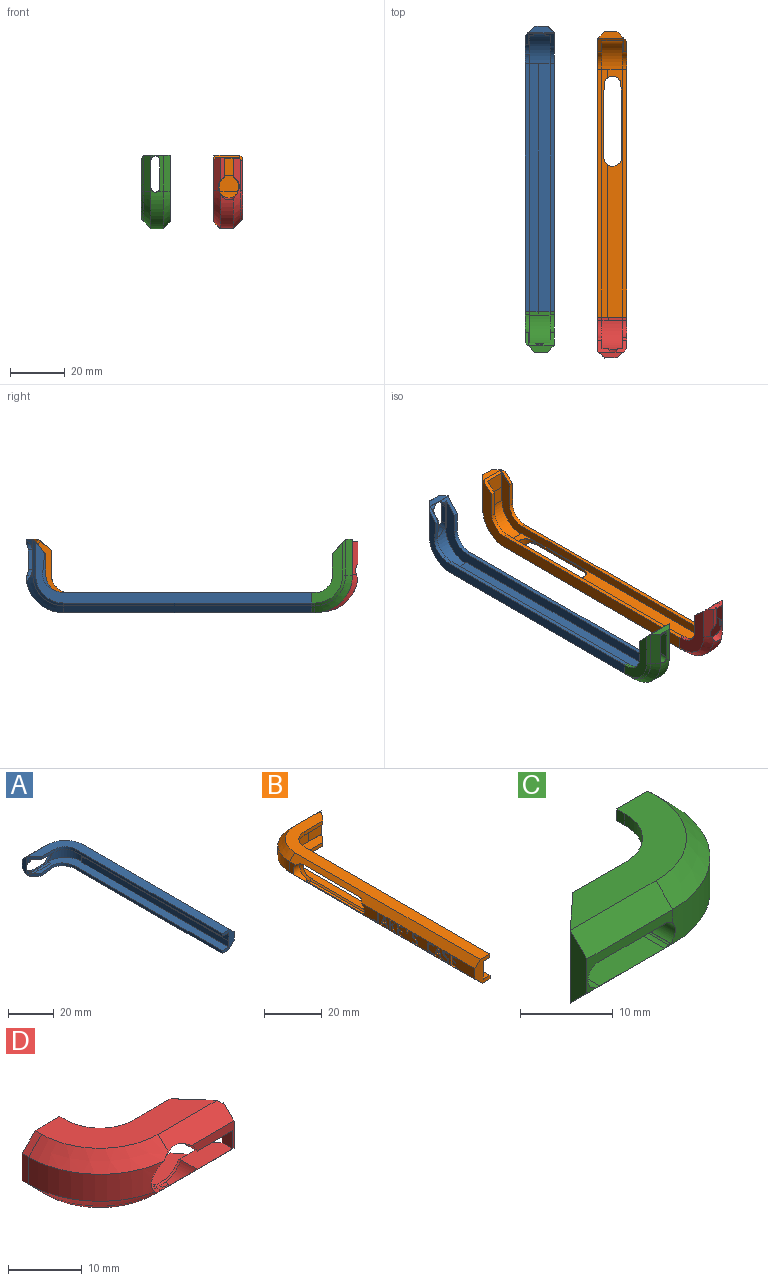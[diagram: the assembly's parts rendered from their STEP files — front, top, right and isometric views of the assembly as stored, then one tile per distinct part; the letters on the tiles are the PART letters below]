
ASSEMBLY  parts=4 mates=2
PART A: 62 faces, bbox 27.2x104.7x11 mm
  f0: bspline ~1.52x1.52mm, area 0mm2, adj f8,f47,f60
  f1: plane 100.84x22.1mm, normal (0,0,-1), area 419.9mm2, adj f2,f3,f4,f27,f28,f54,f55,f56
  f2: plane 5x4.28mm, normal (-0.65,-0.76,0), area 7.6mm2, adj f1,f14,f39,f41,f50,f53,f54,f58
  f3: plane 7.21x1.5mm, normal (0.09,-1,0), area 10.9mm2, adj f1,f4,f5,f17,f58
  f4: cylinder r=5.99mm len=6.33mm, axis (0,0,-1), area 12.5mm2, adj f1,f3,f17,f27
  f5: plane 9.31x5.51mm, normal (-0.65,-0.76,0), area 18.4mm2, adj f3,f6,f7,f11,f12,f15,f16,f17
  f6: cone r=2.27mm half-angle=45deg, axis (0,1,0), area 1.1mm2, adj f5,f9,f12,f47
  f7: plane 10.51x0.06mm, normal (0,-1,0), area 0.7mm2, adj f5,f17,f44,f46
  f8: cone r=2.27mm half-angle=45deg, axis (0,1,0), area 0.6mm2, adj f0,f9,f36,f47
  f9: plane 7.3x0.23mm, normal (0,0.71,-0.71), area 2.4mm2, adj f6,f8,f35,f47
  f10: bspline ~1.51x1.49mm, area 0mm2, adj f26,f42,f44
  f11: cone r=2.27mm half-angle=45deg, axis (0,1,0), area 1.1mm2, adj f5,f12,f25,f43,f46
  f12: cylinder r=3.77mm len=7.53mm, axis (0,1,0), area 28.3mm2, adj f5,f6,f11,f34,f35,f38,f39,f40
  f13: plane 93.02x0.26mm, normal (0,0,-1), area 0.3mm2, adj f31,f32,f51,f52,f57
  f14: plane 0.08x0.04mm, normal (0,0,-1), area 0mm2, adj f2,f20,f39,f41
  f15: plane 101.7x23.07mm, normal (0,0,-1), area 452.5mm2, adj f5,f16,f29,f30,f47,f49,f57,f59
  f16: plane 7.49x1.52mm, normal (0,-1,0), area 11.4mm2, adj f5,f15,f18,f29
  f17: plane 101.7x21.59mm, normal (0,0,1), area 433.3mm2, adj f3,f4,f5,f7,f27,f28,f44,f45
  f18: plane 101.81x24.18mm, normal (0,0,1), area 542.6mm2, adj f5,f16,f24,f29,f30,f37,f38,f57
  f19: plane 0.08x0.06mm, normal (0,0,1), area 0mm2, adj f20,f38,f41
  f20: plane 9.57x2.62mm, normal (-1,0,0), area 18.7mm2, adj f14,f19,f38,f39,f40,f41
  f21: plane 90.62x4.49mm, normal (1,0,0), area 407.2mm2, adj f23,f24,f31,f57
  f22: bspline ~6.5x3.4mm, area 20.5mm2, adj f23,f32,f33,f36,f37,f61
  f23: cylinder r=13.72mm len=13.71mm, axis (0,0,-1), area 86.3mm2, adj f21,f22,f32,f37
  f24: plane 90.62x2.54mm, normal (0.71,0,0.71), area 325.5mm2, adj f18,f21,f37,f57
  f25: plane 7.3x0.27mm, normal (0,0.71,0.71), area 2.8mm2, adj f11,f26,f34,f46
  f26: cone r=2.27mm half-angle=45deg, axis (0,1,0), area 0.6mm2, adj f10,f25,f33,f42,f46
  f27: cylinder r=6.38mm len=3.23mm, axis (0,0,-1), area 5.1mm2, adj f1,f4,f17,f28
  f28: plane 90.62x1.5mm, normal (-1,0,0), area 135.9mm2, adj f1,f17,f27,f57
  f29: cylinder r=6.46mm len=6.46mm, axis (0,0,1), area 15.5mm2, adj f15,f16,f18,f30
  f30: plane 90.62x1.52mm, normal (-1,0,0), area 138.1mm2, adj f15,f18,f29,f57
  f31: plane 90.62x2.54mm, normal (0.71,0,-0.71), area 325.5mm2, adj f13,f21,f32,f57
  f32: cone r=13.72mm half-angle=45deg, axis (0,0,1), area 67.4mm2, adj f13,f22,f23,f31,f39,f51
  f33: cylinder r=3.77mm len=1.9mm, axis (0,1,0), area 2.4mm2, adj f22,f26,f34,f39,f44
  f34: plane 7.3x0.93mm, normal (0,0,1), area 6.8mm2, adj f12,f25,f33,f39
  f35: plane 7.3x2.38mm, normal (0,0,-1), area 17.4mm2, adj f9,f12,f36,f38
  f36: cylinder r=3.77mm len=2.9mm, axis (0,1,0), area 5.3mm2, adj f8,f22,f35,f38,f60
  f37: cone r=13.72mm half-angle=45deg, axis (0,0,-1), area 70.2mm2, adj f18,f22,f23,f24,f38
  f38: plane 13.44x2.92mm, normal (0,0.71,0.71), area 35.3mm2, adj f12,f18,f19,f20,f35,f36,f37,f40
  f39: plane 13.31x2.79mm, normal (0,0.71,-0.71), area 10mm2, adj f2,f12,f14,f20,f32,f33,f34,f40
  f40: plane 4.49x1.55mm, normal (0,1,0), area 1.9mm2, adj f12,f20,f38,f39
  f41: plane 9.57x0.08mm, normal (0.82,-0.58,0), area 1mm2, adj f2,f5,f14,f19,f20,f53
  f42: plane 1.39x0.51mm, normal (0,-1,0), area 0.3mm2, adj f10,f26,f44,f46
  f43: plane 2.28x1.32mm, normal (0,-1,0), area 1.1mm2, adj f5,f11,f46
  f44: plane 2.04x0.57mm, normal (1,0,0), area 0.3mm2, adj f7,f10,f17,f33,f42,f46,f61
  f45: plane 90.62x3.23mm, normal (-1,0,0), area 292.5mm2, adj f17,f48,f57,f59
  f46: plane 12.01x1.3mm, normal (0,0,1), area 14mm2, adj f5,f7,f11,f25,f26,f42,f43,f44
  f47: plane 11.99x1.82mm, normal (0,-1,0), area 6.9mm2, adj f0,f5,f6,f8,f9,f15,f60
  f48: plane 90.62x0.01mm, normal (0,0,1), area 1mm2, adj f45,f49,f57,f59
  f49: plane 90.62x4.32mm, normal (-1,0,0), area 391.6mm2, adj f15,f48,f57,f59
  f50: plane 13.05x0.02mm, normal (0,1,0), area 0.3mm2, adj f2,f39,f51,f54
  f51: cylinder r=11.18mm len=11.2mm, axis (0,0,-1), area 0.3mm2, adj f13,f32,f50,f52,f55
  f52: plane 90.62x0.01mm, normal (1,0,0), area 0.9mm2, adj f13,f51,f56,f57
  f53: plane 4.97x4.27mm, normal (0,0,1), area 0.2mm2, adj f2,f5,f41,f58
  f54: plane 13.05x0.99mm, normal (0,0.71,-0.71), area 17.5mm2, adj f1,f2,f50,f55
  f55: cone r=10.19mm half-angle=45deg, axis (0,0,1), area 23.5mm2, adj f1,f51,f54,f56
  f56: plane 90.62x0.99mm, normal (0.71,0,-0.71), area 127mm2, adj f1,f52,f55,f57
  f57: plane 10.57x7.35mm, normal (0,-1,0), area 38.3mm2, adj f1,f13,f15,f17,f18,f21,f24,f28
  f58: plane 1.27x0.02mm, normal (0.93,-0.38,0), area 0mm2, adj f1,f2,f3,f53
  f59: plane 7.55x0.76mm, normal (0,1,0), area 5.7mm2, adj f15,f17,f45,f48,f49,f61
  f60: plane 1x0.77mm, normal (1,0,0), area 0.6mm2, adj f0,f15,f36,f47,f61
  f61: cylinder r=11.08mm len=11.08mm, axis (0,0,-1), area 120.9mm2, adj f15,f17,f22,f44,f59,f60
PART B: 215 faces, bbox 27.9x105.4x11.6 mm
  f0: cone r=2.74mm half-angle=45deg, axis (-1,0,0), area 1.8mm2, adj f2,f3,f25,f29,f204,f213
  f1: cone r=2.74mm half-angle=45deg, axis (-1,0,0), area 15.3mm2, adj f2,f10,f25,f30,f191,f212,f213,f214
  f2: bspline ~24.21x1.5mm, area 25.1mm2, adj f0,f1,f25,f213
  f3: cone r=4.02mm half-angle=45deg, axis (-1,0,0), area 15.3mm2, adj f0,f9,f201,f202,f203,f204,f211,f213
  f4: plane 10.64x7.55mm, normal (0,-1,0), area 44.6mm2, adj f5,f20,f23,f200,f207,f209
  f5: plane 0.96x0.83mm, normal (-0.65,-0.76,0), area 0mm2, adj f4,f6,f23,f209
  f6: plane 9.3x4.81mm, normal (0.76,-0.65,0), area 18.8mm2, adj f5,f20,f22,f23,f28,f35,f43,f187
  f7: plane 0.96x0.83mm, normal (-0.65,-0.76,0), area 0.5mm2, adj f40,f43,f206
  f8: cylinder r=4.24mm len=0.93mm, axis (-1,0,0), area 0.1mm2, adj f9,f31,f38,f190,f191,f201
  f9: cone r=2.74mm half-angle=45deg, axis (-1,0,0), area 1.5mm2, adj f3,f8,f10,f191,f201,f214
  f10: plane 24.21x0.54mm, normal (-0.71,0,0.71), area 18.6mm2, adj f1,f9,f191,f214
  f11: plane 9.26x4.52mm, normal (-1,0,0), area 22.7mm2, adj f18,f19,f44,f45,f46,f47,f48,f49
  f12: plane 26.97x4.53mm, normal (-1,0,0), area 83.9mm2, adj f18,f19,f30,f80,f81,f82,f83,f84
  f13: plane 8.56x4.55mm, normal (-1,0,0), area 26mm2, adj f18,f19,f75,f76,f77,f78,f90,f91
  f14: plane 15.15x4.52mm, normal (-1,0,0), area 56.3mm2, adj f18,f19,f54,f55,f56,f57,f58,f59
  f15: plane 2.38x1.38mm, normal (-1,0,0), area 2.7mm2, adj f19,f175,f181,f182
  f16: plane 2.38x1.38mm, normal (-1,0,0), area 2.7mm2, adj f19,f161,f167,f168
  f17: plane 2.13x1.8mm, normal (-1,0,0), area 2.3mm2, adj f19,f143,f154,f155
  f18: plane 91.1x3.02mm, normal (-0.71,0,0.71), area 281.3mm2, adj f11,f12,f13,f14,f22,f25,f29,f30
  f19: plane 57.25x2.6mm, normal (-0.71,0,-0.71), area 198.6mm2, adj f11,f12,f13,f14,f15,f16,f17,f24
  f20: plane 100.95x21.93mm, normal (0,0,1), area 381.4mm2, adj f4,f6,f35,f36,f37,f196,f199,f200
  f21: plane 100.81x22.43mm, normal (0,0,-1), area 436.2mm2, adj f35,f36,f37,f192,f193,f194,f195,f196
  f22: plane 101.81x23.53mm, normal (0,0,1), area 545.6mm2, adj f6,f18,f26,f27,f28,f41,f42,f196
  f23: plane 100.94x21.93mm, normal (0,0,-1), area 373.5mm2, adj f4,f5,f6,f26,f27,f28,f196,f199
  f24: plane 57.18x0mm, normal (0,0,-1), area 0mm2, adj f19,f30,f190,f196
  f25: plane 27.07x2.41mm, normal (0,0,-1), area 64.9mm2, adj f0,f1,f2,f18,f29,f30
  f26: plane 90.62x1.52mm, normal (1,0,0), area 138.1mm2, adj f22,f23,f27,f196
  f27: cylinder r=6.45mm len=6.46mm, axis (0,0,1), area 15.5mm2, adj f22,f23,f26,f28
  f28: plane 9.01x1.52mm, normal (0,-1,0), area 13.7mm2, adj f6,f22,f23,f27
  f29: cylinder r=4.24mm len=2.17mm, axis (-1,0,0), area 0.1mm2, adj f0,f18,f25,f202
  f30: cylinder r=4.24mm len=8.05mm, axis (-1,0,0), area 26.5mm2, adj f1,f12,f18,f19,f24,f25,f190,f191
  f31: plane 24.24x17.98mm, normal (0,0,-1), area 0.1mm2, adj f8,f38,f39,f40,f188,f189,f190,f197
  f32: plane 13.06x4.49mm, normal (0,1,0), area 58.7mm2, adj f34,f40,f41,f43
  f33: plane 4.49x3mm, normal (-1,0,0), area 9.1mm2, adj f18,f34,f38,f203
  f34: cylinder r=13.72mm len=13.73mm, axis (0,0,-1), area 96.9mm2, adj f32,f33,f39,f42
  f35: plane 8.93x1.5mm, normal (0,-1,0), area 13.4mm2, adj f6,f20,f21,f37,f192
  f36: plane 90.62x1.5mm, normal (1,0,0), area 135.9mm2, adj f20,f21,f37,f196
  f37: cylinder r=6.38mm len=6.38mm, axis (0,0,-1), area 15mm2, adj f20,f21,f35,f36
  f38: plane 7.82x3.57mm, normal (-0.71,0,-0.71), area 12.4mm2, adj f8,f31,f33,f39,f201,f203
  f39: cone r=13.72mm half-angle=45deg, axis (0,0,1), area 70.3mm2, adj f31,f34,f38,f40
  f40: plane 13.06x2.54mm, normal (0,0.71,-0.71), area 46.5mm2, adj f7,f31,f32,f39,f43,f187,f197,f206
  f41: plane 13.06x2.54mm, normal (0,0.71,0.71), area 45.9mm2, adj f22,f32,f42,f43,f198,f205
  f42: cone r=13.72mm half-angle=45deg, axis (0,0,-1), area 70.3mm2, adj f18,f22,f34,f41
  f43: plane 9.57x2.54mm, normal (1,0,0), area 17.9mm2, adj f6,f7,f32,f40,f41,f198
  f44: extruded ~1.07x0.76mm, area 0.9mm2, adj f11,f18,f45,f63,f64
  f45: extruded ~0.83x0.76mm, area 0.7mm2, adj f11,f44,f46,f64
  f46: extruded ~0.8x0.76mm, area 0.7mm2, adj f11,f45,f47,f64
  f47: extruded ~0.91x0.76mm, area 0.8mm2, adj f11,f46,f48,f64
  f48: extruded ~0.87x0.76mm, area 0.7mm2, adj f11,f47,f49,f64
  f49: extruded ~0.76x0.49mm, area 0.4mm2, adj f11,f48,f50,f64
  f50: extruded ~1.07x0.76mm, area 1.1mm2, adj f11,f49,f51,f64
  f51: extruded ~1.26x0.76mm, area 1mm2, adj f11,f50,f52,f64
  f52: plane 0.76x0.54mm, normal (0,-1,0), area 0.4mm2, adj f11,f51,f53,f64
  f53: extruded ~1.26x0.76mm, area 1mm2, adj f11,f19,f52,f54,f64
  f54: extruded ~1.2x0.76mm, area 0.9mm2, adj f14,f19,f53,f55,f64
  f55: extruded ~0.92x0.76mm, area 0.8mm2, adj f14,f54,f56,f64
  f56: extruded ~0.76x0.73mm, area 0.6mm2, adj f14,f55,f57,f64
  f57: extruded ~1x0.76mm, area 0.9mm2, adj f14,f56,f58,f64
  f58: extruded ~0.82x0.76mm, area 0.7mm2, adj f14,f57,f59,f64
  f59: extruded ~0.76x0.5mm, area 0.4mm2, adj f14,f58,f60,f64
  f60: extruded ~0.89x0.76mm, area 1mm2, adj f14,f59,f61,f64
  f61: extruded ~1.1x0.76mm, area 0.9mm2, adj f14,f60,f62,f64
  f62: plane 0.76x0.5mm, normal (0,0.93,0.36), area 0.4mm2, adj f14,f61,f63,f64
  f63: extruded ~1.27x0.76mm, area 1mm2, adj f14,f18,f44,f62,f64
  f64: plane 4.58x2.88mm, normal (-1,0,0), area 5mm2, adj f44,f45,f46,f47,f48,f49,f50,f51
  f65: extruded ~1.09x0.76mm, area 0.8mm2, adj f11,f19,f66,f78,f79
  f66: plane 0.76x0.49mm, normal (0,1,0), area 0.4mm2, adj f11,f65,f67,f79
  f67: extruded ~1x0.76mm, area 0.8mm2, adj f11,f66,f68,f79
  f68: extruded ~1.07x0.76mm, area 0.9mm2, adj f11,f67,f69,f79
  f69: extruded ~1.33x0.76mm, area 1.1mm2, adj f11,f68,f70,f79
  f70: extruded ~1.31x0.76mm, area 1.1mm2, adj f11,f69,f71,f79
  f71: extruded ~1.05x0.76mm, area 0.9mm2, adj f11,f70,f72,f79
  f72: extruded ~0.93x0.76mm, area 0.7mm2, adj f11,f71,f73,f79
  f73: plane 0.76x0.48mm, normal (0,0.89,0.45), area 0.4mm2, adj f11,f72,f74,f79
  f74: extruded ~1.17x0.76mm, area 0.9mm2, adj f11,f18,f73,f75,f79
  f75: extruded ~1.49x0.76mm, area 1.3mm2, adj f13,f18,f74,f76,f79
  f76: extruded ~1.67x0.76mm, area 1.4mm2, adj f13,f75,f77,f79
  f77: extruded ~1.7x0.76mm, area 1.4mm2, adj f13,f76,f78,f79
  f78: extruded ~1.44x0.76mm, area 1.2mm2, adj f13,f19,f65,f77,f79
  f79: plane 4.58x3.2mm, normal (-1,0,0), area 4.5mm2, adj f65,f66,f67,f68,f69,f70,f71,f72
  f80: extruded ~1.07x0.76mm, area 0.9mm2, adj f12,f18,f81,f99,f100
  f81: extruded ~0.83x0.76mm, area 0.7mm2, adj f12,f80,f82,f100
  f82: extruded ~0.8x0.76mm, area 0.7mm2, adj f12,f81,f83,f100
  f83: extruded ~0.91x0.76mm, area 0.8mm2, adj f12,f82,f84,f100
  f84: extruded ~0.87x0.76mm, area 0.7mm2, adj f12,f83,f85,f100
  f85: extruded ~0.76x0.49mm, area 0.4mm2, adj f12,f84,f86,f100
  f86: extruded ~1.07x0.76mm, area 1.1mm2, adj f12,f85,f87,f100
  f87: extruded ~1.26x0.76mm, area 1mm2, adj f12,f86,f88,f100
  f88: plane 0.76x0.54mm, normal (0,-1,0), area 0.4mm2, adj f12,f87,f89,f100
  f89: extruded ~1.26x0.76mm, area 1mm2, adj f12,f19,f88,f90,f100
  f90: extruded ~1.2x0.76mm, area 0.9mm2, adj f13,f19,f89,f91,f100
  f91: extruded ~0.92x0.76mm, area 0.8mm2, adj f13,f90,f92,f100
  f92: extruded ~0.76x0.73mm, area 0.6mm2, adj f13,f91,f93,f100
  f93: extruded ~1x0.76mm, area 0.9mm2, adj f13,f92,f94,f100
  f94: extruded ~0.82x0.76mm, area 0.7mm2, adj f13,f93,f95,f100
  f95: extruded ~0.76x0.5mm, area 0.4mm2, adj f13,f94,f96,f100
  f96: extruded ~0.89x0.76mm, area 1mm2, adj f13,f95,f97,f100
  f97: extruded ~1.1x0.76mm, area 0.9mm2, adj f13,f96,f98,f100
  f98: plane 0.76x0.5mm, normal (0,0.93,0.36), area 0.4mm2, adj f13,f97,f99,f100
  f99: extruded ~1.27x0.76mm, area 1mm2, adj f13,f18,f80,f98,f100
  f100: plane 4.58x2.88mm, normal (-1,0,0), area 5mm2, adj f80,f81,f82,f83,f84,f85,f86,f87
  f101: extruded ~1.15x0.76mm, area 0.9mm2, adj f12,f19,f102,f110,f111
  f102: extruded ~1.05x0.76mm, area 0.9mm2, adj f12,f101,f103,f111
  f103: plane 3.08x0.76mm, normal (0,1,0), area 2.3mm2, adj f12,f102,f104,f111
  f104: plane 0.76x0.57mm, normal (0,0,-1), area 0.4mm2, adj f12,f103,f105,f111
  f105: plane 3.09x0.76mm, normal (0,-1,0), area 2.4mm2, adj f12,f104,f106,f111
  f106: extruded ~0.76x0.69mm, area 0.6mm2, adj f12,f105,f107,f111
  f107: extruded ~0.77x0.76mm, area 0.6mm2, adj f12,f106,f108,f111
  f108: extruded ~0.94x0.76mm, area 0.7mm2, adj f12,f107,f109,f111
  f109: plane 0.76x0.51mm, normal (0,-1,0), area 0.4mm2, adj f12,f108,f110,f111
  f110: extruded ~0.99x0.76mm, area 0.8mm2, adj f12,f19,f101,f109,f111
  f111: plane 4.52x2.57mm, normal (-1,0,0), area 3.3mm2, adj f101,f102,f103,f104,f105,f106,f107,f108
  f112: plane 4.46x0.76mm, normal (0,-1,0), area 3.4mm2, adj f12,f113,f123,f124
  f113: plane 2.57x0.76mm, normal (0,0,1), area 2mm2, adj f19,f112,f114,f124
  f114: plane 0.76x0.5mm, normal (0,1,0), area 0.4mm2, adj f12,f113,f115,f124
  f115: plane 2x0.76mm, normal (0,0,-1), area 1.5mm2, adj f12,f114,f116,f124
  f116: plane 1.58x0.76mm, normal (0,1,0), area 1.2mm2, adj f12,f115,f117,f124
  f117: plane 1.88x0.76mm, normal (0,0,1), area 1.4mm2, adj f12,f116,f118,f124
  f118: plane 0.76x0.49mm, normal (0,1,0), area 0.4mm2, adj f12,f117,f119,f124
  f119: plane 1.88x0.76mm, normal (0,0,-1), area 1.4mm2, adj f12,f118,f120,f124
  f120: plane 1.38x0.76mm, normal (0,1,0), area 1mm2, adj f12,f119,f121,f124
  f121: plane 2x0.76mm, normal (0,0,1), area 1.5mm2, adj f12,f120,f122,f124
  f122: plane 0.76x0.5mm, normal (0,1,0), area 0.4mm2, adj f12,f121,f123,f124
  f123: plane 2.57x0.76mm, normal (0,0,-1), area 2mm2, adj f12,f112,f122,f124
  f124: plane 4.46x2.57mm, normal (-1,0,0), area 5.5mm2, adj f112,f113,f114,f115,f116,f117,f118,f119
  f125: plane 1.61x0.76mm, normal (0,1,0.08), area 1.2mm2, adj f12,f126,f128,f129
  f126: plane 0.76x0.72mm, normal (0,0,-1), area 0.6mm2, adj f12,f125,f127,f129
  f127: plane 1.61x0.76mm, normal (0,-1,0.08), area 1.2mm2, adj f12,f126,f128,f129
  f128: plane 0.76x0.47mm, normal (0,0,1), area 0.4mm2, adj f12,f125,f127,f129
  f129: plane 1.61x0.72mm, normal (-1,0,0), area 1mm2, adj f125,f126,f127,f128
  f130: plane 4.46x0.76mm, normal (0,-1,0), area 3.4mm2, adj f14,f131,f141,f142
  f131: plane 2.57x0.76mm, normal (0,0,1), area 2mm2, adj f19,f130,f132,f142
  f132: plane 0.76x0.5mm, normal (0,1,0), area 0.4mm2, adj f14,f131,f133,f142
  f133: plane 2x0.76mm, normal (0,0,-1), area 1.5mm2, adj f14,f132,f134,f142
  f134: plane 1.58x0.76mm, normal (0,1,0), area 1.2mm2, adj f14,f133,f135,f142
  f135: plane 1.88x0.76mm, normal (0,0,1), area 1.4mm2, adj f14,f134,f136,f142
  f136: plane 0.76x0.49mm, normal (0,1,0), area 0.4mm2, adj f14,f135,f137,f142
  f137: plane 1.88x0.76mm, normal (0,0,-1), area 1.4mm2, adj f14,f136,f138,f142
  f138: plane 1.38x0.76mm, normal (0,1,0), area 1mm2, adj f14,f137,f139,f142
  f139: plane 2x0.76mm, normal (0,0,1), area 1.5mm2, adj f14,f138,f140,f142
  f140: plane 0.76x0.5mm, normal (0,1,0), area 0.4mm2, adj f14,f139,f141,f142
  f141: plane 2.57x0.76mm, normal (0,0,-1), area 2mm2, adj f14,f130,f140,f142
  f142: plane 4.46x2.57mm, normal (-1,0,0), area 5.5mm2, adj f130,f131,f132,f133,f134,f135,f136,f137
  f143: plane 2.13x1.37mm, normal (0,-0.84,0.54), area 1.9mm2, adj f17,f144,f155,f156
  f144: plane 0.76x0.64mm, normal (0,0,1), area 0.5mm2, adj f19,f143,f145,f156
  f145: plane 2.51x1.64mm, normal (0,0.84,-0.55), area 2.3mm2, adj f12,f144,f146,f156
  f146: plane 1.94x1.59mm, normal (0,0.77,0.63), area 1.9mm2, adj f12,f145,f147,f156
  f147: plane 0.76x0.64mm, normal (0,0,-1), area 0.5mm2, adj f12,f146,f148,f156
  f148: plane 1.72x1.38mm, normal (0,-0.78,-0.63), area 1.7mm2, adj f12,f147,f149,f156
  f149: plane 0.76x0.51mm, normal (0,-0.81,-0.58), area 0.5mm2, adj f12,f148,f150,f156
  f150: plane 2.23x0.76mm, normal (0,1,0), area 1.7mm2, adj f12,f149,f151,f156
  f151: plane 0.76x0.57mm, normal (0,0,-1), area 0.4mm2, adj f12,f150,f152,f156
  f152: plane 4.46x0.76mm, normal (0,-1,0), area 3.4mm2, adj f12,f151,f153,f156
  f153: plane 0.76x0.57mm, normal (0,0,1), area 0.4mm2, adj f19,f152,f154,f156
  f154: plane 1.78x0.76mm, normal (0,1,0), area 1.4mm2, adj f17,f153,f155,f156
  f155: plane 0.76x0.43mm, normal (0,0.63,0.78), area 0.4mm2, adj f17,f143,f154,f156
  f156: plane 4.46x3.01mm, normal (-1,0,0), area 5.5mm2, adj f143,f144,f145,f146,f147,f148,f149,f150
  f157: plane 1.29x0.76mm, normal (0,-0.95,0.3), area 1mm2, adj f158,f169,f170,f185
  f158: plane 1.17x0.76mm, normal (0,0,-1), area 0.9mm2, adj f157,f159,f170,f185
  f159: plane 1.42x0.76mm, normal (0,0.96,0.29), area 1.1mm2, adj f158,f160,f170,f185
  f160: extruded ~0.76x0.56mm, area 0.4mm2, adj f159,f169,f170,f185
  f161: plane 1.38x0.76mm, normal (0,-0.95,0.3), area 1.1mm2, adj f16,f162,f168,f170
  f162: plane 0.76x0.59mm, normal (0,0,1), area 0.4mm2, adj f19,f161,f163,f170
  f163: plane 4.47x1.48mm, normal (0,0.95,-0.31), area 3.6mm2, adj f12,f162,f164,f170
  f164: plane 0.76x0.59mm, normal (0,0,-1), area 0.5mm2, adj f12,f163,f165,f170
  f165: plane 4.47x1.47mm, normal (0,-0.95,-0.31), area 3.6mm2, adj f12,f164,f166,f170
  f166: plane 0.76x0.58mm, normal (0,0,1), area 0.4mm2, adj f19,f165,f167,f170
  f167: plane 1.38x0.76mm, normal (0,0.95,0.31), area 1.1mm2, adj f16,f166,f168,f170
  f168: plane 1.5x0.76mm, normal (0,0,1), area 1.1mm2, adj f16,f161,f167,f170
  f169: extruded ~0.76x0.69mm, area 0.5mm2, adj f157,f160,f170,f185
  f170: plane 4.47x3.55mm, normal (-1,0,0), area 5.5mm2, adj f157,f158,f159,f160,f161,f162,f163,f164
  f171: plane 1.29x0.76mm, normal (0,-0.95,0.3), area 1mm2, adj f172,f183,f184,f186
  f172: plane 1.17x0.76mm, normal (0,0,-1), area 0.9mm2, adj f171,f173,f184,f186
  f173: plane 1.42x0.76mm, normal (0,0.96,0.29), area 1.1mm2, adj f172,f174,f184,f186
  f174: extruded ~0.76x0.56mm, area 0.4mm2, adj f173,f183,f184,f186
  f175: plane 1.38x0.76mm, normal (0,-0.95,0.3), area 1.1mm2, adj f15,f176,f182,f184
  f176: plane 0.76x0.59mm, normal (0,0,1), area 0.4mm2, adj f19,f175,f177,f184
  f177: plane 4.47x1.48mm, normal (0,0.95,-0.31), area 3.6mm2, adj f11,f176,f178,f184
  f178: plane 0.76x0.59mm, normal (0,0,-1), area 0.5mm2, adj f11,f177,f179,f184
  f179: plane 4.47x1.47mm, normal (0,-0.95,-0.31), area 3.6mm2, adj f11,f178,f180,f184
  f180: plane 0.76x0.58mm, normal (0,0,1), area 0.4mm2, adj f19,f179,f181,f184
  f181: plane 1.38x0.76mm, normal (0,0.95,0.31), area 1.1mm2, adj f15,f180,f182,f184
  f182: plane 1.5x0.76mm, normal (0,0,1), area 1.1mm2, adj f15,f175,f181,f184
  f183: extruded ~0.76x0.69mm, area 0.5mm2, adj f171,f174,f184,f186
  f184: plane 4.47x3.55mm, normal (-1,0,0), area 5.5mm2, adj f171,f172,f173,f174,f175,f176,f177,f178
  f185: plane 1.98x1.17mm, normal (-1,0,0), area 1.1mm2, adj f157,f158,f159,f160,f169
  f186: plane 1.98x1.17mm, normal (-1,0,0), area 1.1mm2, adj f171,f172,f173,f174,f183
  f187: plane 5.08x4.16mm, normal (0,0,1), area 0.7mm2, adj f6,f40,f188,f192,f197,f206
  f188: plane 13.1x0.28mm, normal (0,1,0), area 0.1mm2, adj f31,f187,f189,f192,f195,f197
  f189: cylinder r=11.18mm len=11.18mm, axis (0,0,-1), area 0.2mm2, adj f31,f188,f190,f194
  f190: plane 90.62x0.28mm, normal (-1,0,0), area 8.2mm2, adj f8,f24,f30,f31,f189,f191,f193,f196
  f191: plane 28.01x1.08mm, normal (0,0,1), area 29.7mm2, adj f1,f8,f9,f10,f30,f190
  f192: plane 4.81x4.16mm, normal (0.76,-0.65,0), area 7.4mm2, adj f21,f35,f187,f188,f195
  f193: plane 90.62x0.99mm, normal (-0.71,0,-0.71), area 127mm2, adj f21,f190,f194,f196
  f194: cone r=10.19mm half-angle=45deg, axis (0,0,1), area 23.5mm2, adj f21,f189,f193,f195
  f195: plane 13.1x0.99mm, normal (0,0.71,-0.71), area 17.7mm2, adj f21,f188,f192,f194
  f196: plane 10.57x7.35mm, normal (0,-1,0), area 44.1mm2, adj f14,f18,f19,f20,f21,f22,f23,f24
  f197: plane 0.32x0.27mm, normal (0.65,0.76,0), area 0.1mm2, adj f31,f40,f187,f188
  f198: plane 0.96x0.83mm, normal (-0.65,-0.76,0), area 0.5mm2, adj f41,f43,f205
  f199: plane 7.55x0.76mm, normal (0,1,0), area 5.7mm2, adj f20,f23,f200,f211,f213,f214
  f200: cylinder r=10.32mm len=10.32mm, axis (0,0,-1), area 122.4mm2, adj f4,f20,f23,f199
  f201: plane 1.15x0.8mm, normal (0,0,1), area 0.6mm2, adj f3,f8,f9,f38,f203
  f202: plane 2.24x0.94mm, normal (0,0,-1), area 2.1mm2, adj f3,f18,f29,f203,f204
  f203: cylinder r=3.87mm len=7.75mm, axis (-1,0,0), area 34mm2, adj f3,f18,f33,f38,f201,f202
  f204: plane 0.22x0.03mm, normal (-1,0,0), area 0mm2, adj f0,f3,f202
  f205: plane 1.67x1.65mm, normal (0.39,0.46,0.8), area 1.7mm2, adj f6,f22,f41,f198
  f206: plane 1.44x1.38mm, normal (0.39,0.46,-0.8), area 1.2mm2, adj f6,f7,f40,f187
  f207: plane 7.53x0.01mm, normal (1,0,0), area 0.1mm2, adj f4,f208,f209
  f208: plane 7.53x6.43mm, normal (0,-1,0), area 48.4mm2, adj f6,f207,f209,f210
  f209: plane 6.43x0.84mm, normal (0,0,-1), area 0.8mm2, adj f4,f5,f6,f207,f208
  f210: plane 6.44x0.85mm, normal (0,0,1), area 0.8mm2, adj f6,f20,f208
  f211: plane 3.14x0.01mm, normal (0,0,1), area 0mm2, adj f3,f199,f213,f214
  f212: plane 55.67x0.01mm, normal (0,0,1), area 0.6mm2, adj f1,f196,f213,f214
  f213: plane 90.62x2.23mm, normal (1,0,0), area 157.4mm2, adj f0,f1,f2,f3,f23,f196,f199,f211
  f214: plane 90.62x5.32mm, normal (1,0,0), area 323.7mm2, adj f1,f3,f9,f10,f20,f196,f199,f211
PART C: 54 faces, bbox 26.8x15x10.6 mm
  f0: plane 12.12x2.83mm, normal (0,1,0), area 27.9mm2, adj f4,f6,f20,f42,f45,f46,f52
  f1: cylinder r=0.61mm len=3.41mm, axis (0,-1,0), area 0.9mm2, adj f2,f9,f10,f47
  f2: cylinder r=1.61mm len=3.41mm, axis (0,-1,0), area 2.3mm2, adj f1,f3,f9,f10
  f3: plane 9.82x3.41mm, normal (0,0,1), area 33.4mm2, adj f2,f6,f10,f12
  f4: plane 9.83x3.41mm, normal (0,0,-1), area 33.5mm2, adj f0,f6,f8,f46
  f5: plane 12.12x1.27mm, normal (0,0,1), area 14.5mm2, adj f10,f15,f16,f20
  f6: cylinder r=1.62mm len=3.41mm, axis (0,-1,0), area 17mm2, adj f0,f3,f4,f8,f10,f12,f20
  f7: plane 5.25x4.81mm, normal (0,0,1), area 0mm2, adj f11,f13,f19,f20
  f8: plane 13.06x4.49mm, normal (0,-1,0), area 18.4mm2, adj f4,f6,f12,f18,f19,f22,f45,f46
  f9: plane 1.28x0.55mm, normal (0,-1,0), area 0.2mm2, adj f1,f2,f12,f22,f45,f47
  f10: plane 12.12x2.57mm, normal (0,1,0), area 24.8mm2, adj f1,f2,f3,f5,f6,f15,f20,f45
  f11: plane 13.07x0.28mm, normal (0,-1,0), area 0.1mm2, adj f7,f13,f14,f19,f27,f43
  f12: plane 13.08x2.56mm, normal (0,-0.71,-0.71), area 46.9mm2, adj f3,f6,f8,f9,f19,f26,f43
  f13: plane 5.25x4.81mm, normal (-0.68,0.74,0), area 8.3mm2, adj f7,f11,f14,f17,f41
  f14: plane 13.07x0.99mm, normal (0,-0.71,-0.71), area 17.6mm2, adj f11,f13,f28,f41
  f15: plane 2.58x2.03mm, normal (1,0,0), area 2mm2, adj f5,f10,f16,f40,f45,f51
  f16: plane 10.73x0.01mm, normal (0,1,0), area 0.1mm2, adj f5,f15,f20,f40
  f17: plane 7.82x1.5mm, normal (0,1,0), area 11.7mm2, adj f13,f20,f24,f40,f41
  f18: plane 13.06x2.54mm, normal (0,-0.71,0.71), area 46.9mm2, adj f8,f19,f23,f33
  f19: plane 9.57x2.54mm, normal (-1,0,0), area 17.9mm2, adj f7,f8,f11,f12,f18,f20,f33,f43
  f20: plane 9.3x5.24mm, normal (-0.68,0.74,0), area 19.9mm2, adj f0,f5,f6,f7,f10,f16,f17,f19
  f21: plane 7.91x1.52mm, normal (0,1,0), area 12.1mm2, adj f20,f25,f33,f42
  f22: cylinder r=13.72mm len=13.73mm, axis (0,0,-1), area 96.3mm2, adj f8,f9,f23,f26,f32,f45
  f23: cone r=13.72mm half-angle=45deg, axis (0,0,-1), area 70.3mm2, adj f18,f22,f30,f33
  f24: cylinder r=6.38mm len=6.38mm, axis (0,0,-1), area 15mm2, adj f17,f39,f40,f41
  f25: cylinder r=6.46mm len=6.46mm, axis (0,0,1), area 15.5mm2, adj f21,f29,f33,f42
  f26: cone r=13.72mm half-angle=45deg, axis (0,0,1), area 70.3mm2, adj f12,f22,f31,f43
  f27: cylinder r=11.18mm len=11.18mm, axis (0,0,-1), area 0.2mm2, adj f11,f28,f35,f43
  f28: cone r=10.19mm half-angle=45deg, axis (0,0,1), area 23.5mm2, adj f14,f27,f34,f41
  f29: plane 1.52x1.24mm, normal (-1,0,0), area 1.9mm2, adj f25,f33,f42,f44
  f30: plane 2.54x2.54mm, normal (0.71,0,0.71), area 4.5mm2, adj f23,f32,f33,f44
  f31: plane 2.54x2.54mm, normal (0.71,0,-0.71), area 4.5mm2, adj f26,f32,f43,f44
  f32: plane 4.49x1.24mm, normal (1,0,0), area 5.6mm2, adj f22,f30,f31,f44
  f33: plane 24.24x12.42mm, normal (0,0,1), area 120.9mm2, adj f18,f19,f20,f21,f23,f25,f29,f30
  f34: plane 1.24x0.99mm, normal (0.71,0,-0.71), area 1.7mm2, adj f28,f35,f41,f44
  f35: plane 1.24x0.01mm, normal (1,0,0), area 0mm2, adj f27,f34,f43,f44
  f36: plane 4.32x1.24mm, normal (-1,0,0), area 5.4mm2, adj f37,f42,f44,f48
  f37: plane 1.24x0.01mm, normal (0,0,1), area 0mm2, adj f36,f38,f44,f48
  f38: plane 3.23x1.24mm, normal (-1,0,0), area 4mm2, adj f37,f40,f44,f48
  f39: plane 1.5x1.24mm, normal (-1,0,0), area 1.9mm2, adj f24,f40,f41,f44
  f40: plane 21.81x12.32mm, normal (0,0,1), area 94.2mm2, adj f15,f16,f17,f20,f24,f38,f39,f44
  f41: plane 22.18x11.43mm, normal (0,0,-1), area 92.2mm2, adj f13,f14,f17,f24,f28,f34,f39,f44
  f42: plane 23.2x12.32mm, normal (0,0,-1), area 107.2mm2, adj f0,f20,f21,f25,f29,f36,f44,f48
  f43: plane 24.24x12.42mm, normal (0,0,-1), area 0.1mm2, adj f11,f12,f19,f26,f27,f31,f35,f44
  f44: plane 10.57x7.35mm, normal (0,1,0), area 38.3mm2, adj f29,f30,f31,f32,f33,f34,f35,f36
  f45: cylinder r=1.66mm len=3.41mm, axis (0,-1,0), area 14.4mm2, adj f0,f8,f9,f10,f15,f22,f46,f47
  f46: plane 3.41x0.05mm, normal (1,0,0), area 0.2mm2, adj f0,f4,f8,f45
  f47: plane 3.41x0.04mm, normal (0.84,0,0.55), area 0.2mm2, adj f1,f9,f10,f45
  f48: plane 7.55x0.76mm, normal (0,-1,0), area 5.7mm2, adj f36,f37,f38,f40,f42,f51
  f49: bspline ~0.76x0mm, area 0mm2, adj f45,f51,f53
  f50: bspline ~0.76x0.04mm, area 0mm2, adj f45,f51,f53
  f51: cylinder r=11.08mm len=11.08mm, axis (0,0,-1), area 130.8mm2, adj f15,f40,f42,f45,f48,f49,f50,f52
  f52: plane 2.83x0.76mm, normal (1,0,0), area 2.2mm2, adj f0,f42,f45,f51
  f53: bspline ~2.04x0.77mm, area 1.7mm2, adj f45,f49,f50,f51
PART D: 60 faces, bbox 25.9x15.1x10.7 mm
  f0: bspline ~1.15x1.03mm, area 0mm2, adj f11,f45,f57
  f1: plane 22.52x12.42mm, normal (0,0,1), area 114.8mm2, adj f10,f22,f23,f24,f26,f34,f36,f44
  f2: plane 21.62x12.32mm, normal (0,0,-1), area 102.5mm2, adj f10,f24,f26,f34,f40,f44,f45,f46
  f3: plane 7.07x3.41mm, normal (0,0,-1), area 22.4mm2, adj f11,f16,f17,f44,f45,f50
  f4: plane 7.08x3.41mm, normal (0,0,1), area 22.4mm2, adj f6,f15,f19,f38,f39,f50
  f5: plane 11.33x0.99mm, normal (0,-0.71,-0.71), area 15.2mm2, adj f7,f9,f29,f38
  f6: plane 11.79x2.55mm, normal (0,-0.71,-0.71), area 29.3mm2, adj f4,f8,f19,f25,f38,f51
  f7: plane 11.32x0.01mm, normal (0,-1,0), area 0.1mm2, adj f5,f8,f28,f38
  f8: plane 22.52x12.42mm, normal (0,0,-1), area 0mm2, adj f6,f7,f10,f25,f28,f32,f35,f38
  f9: plane 20.62x11.43mm, normal (0,0,-1), area 87.7mm2, adj f5,f10,f21,f27,f29,f30,f31,f38
  f10: plane 10.57x7.35mm, normal (0,1,0), area 38.3mm2, adj f1,f2,f8,f9,f30,f31,f32,f33
  f11: cone r=2.83mm half-angle=45deg, axis (0,-1,0), area 1.9mm2, adj f0,f3,f17,f45
  f12: bspline ~1.15x1.03mm, area 0mm2, adj f15,f43,f58
  f13: plane 1.1x0.04mm, normal (0,-1,0), area 0mm2, adj f14,f19
  f14: plane 1.22x0.79mm, normal (0,0,1), area 0.7mm2, adj f13,f15,f19
  f15: cone r=2.83mm half-angle=45deg, axis (0,-1,0), area 1.9mm2, adj f4,f12,f14,f19,f33,f39,f43
  f16: plane 8.18x4.5mm, normal (0,-1,0), area 11.8mm2, adj f3,f17,f22,f50,f51,f55
  f17: cylinder r=3.83mm len=4.97mm, axis (0,-1,0), area 16.3mm2, adj f3,f11,f16,f18,f22,f57
  f18: bspline ~7.09x3.42mm, area 22.5mm2, adj f17,f19,f20,f23,f25,f59
  f19: cylinder r=3.83mm len=4.97mm, axis (0,-1,0), area 8.2mm2, adj f4,f6,f13,f14,f15,f18,f58
  f20: cylinder r=13.72mm len=13.66mm, axis (0,0,-1), area 83.5mm2, adj f18,f23,f25,f37
  f21: plane 7.13x1.5mm, normal (0,1,0), area 10.7mm2, adj f9,f27,f33,f48
  f22: plane 12.04x2.54mm, normal (0,-0.71,0.71), area 39.4mm2, adj f1,f16,f17,f23,f44,f54,f55
  f23: cone r=13.72mm half-angle=45deg, axis (0,0,-1), area 69.7mm2, adj f1,f18,f20,f22,f36
  f24: plane 7.2x1.52mm, normal (0,1,0), area 11mm2, adj f1,f2,f26,f49
  f25: cone r=13.72mm half-angle=45deg, axis (0,0,1), area 65.2mm2, adj f6,f8,f18,f20,f35
  f26: cylinder r=6.46mm len=6.46mm, axis (0,0,1), area 15.5mm2, adj f1,f2,f24,f34
  f27: cylinder r=6.38mm len=6.38mm, axis (0,0,-1), area 15mm2, adj f9,f21,f30,f33
  f28: cylinder r=11.18mm len=11.19mm, axis (0,0,-1), area 0.2mm2, adj f7,f8,f29,f32
  f29: cone r=10.19mm half-angle=45deg, axis (0,0,1), area 23.5mm2, adj f5,f9,f28,f31
  f30: plane 1.5x1.24mm, normal (1,0,0), area 1.9mm2, adj f9,f10,f27,f33
  f31: plane 1.24x0.99mm, normal (-0.71,0,-0.71), area 1.7mm2, adj f9,f10,f29,f32
  f32: plane 1.24x0.01mm, normal (-1,0,0), area 0mm2, adj f8,f10,f28,f31
  f33: plane 21.73x12.43mm, normal (0,0,1), area 104mm2, adj f10,f15,f21,f27,f30,f38,f39,f42
  f34: plane 1.52x1.24mm, normal (1,0,0), area 1.9mm2, adj f1,f2,f10,f26
  f35: plane 2.54x2.54mm, normal (-0.71,0,-0.71), area 4.5mm2, adj f8,f10,f25,f37
  f36: plane 2.54x2.54mm, normal (-0.71,0,0.71), area 4.5mm2, adj f1,f10,f23,f37
  f37: plane 4.49x1.24mm, normal (-1,0,0), area 5.6mm2, adj f10,f20,f35,f36
  f38: plane 4.45x4.08mm, normal (0.74,0.68,0), area 11.3mm2, adj f4,f5,f6,f7,f8,f9,f33,f39
  f39: plane 8.55x2.04mm, normal (0,1,0), area 13.7mm2, adj f4,f15,f33,f38
  f40: plane 2.23x1.24mm, normal (1,0,0), area 2.8mm2, adj f2,f10,f41,f56
  f41: plane 1.24x0.01mm, normal (0,0,1), area 0mm2, adj f10,f40,f42,f56
  f42: plane 5.32x1.24mm, normal (1,0,0), area 6.6mm2, adj f10,f33,f41,f56
  f43: plane 0.92x0.26mm, normal (0,1,0), area 0.1mm2, adj f12,f15,f33,f58
  f44: plane 4.36x4mm, normal (0.74,0.68,0), area 13.4mm2, adj f1,f2,f3,f22,f45,f46,f54
  f45: plane 10.54x2.48mm, normal (0,1,0), area 18.4mm2, adj f0,f2,f3,f11,f44,f57
  f46: plane 1.52x0.06mm, normal (0.68,-0.74,0), area 0.1mm2, adj f1,f2,f44,f49
  f47: plane 1.5x0.07mm, normal (0.68,-0.74,0), area 0.1mm2, adj f9,f33,f38,f48
  f48: plane 1.5x0.8mm, normal (0.78,0.63,0), area 1.5mm2, adj f9,f21,f33,f47
  f49: plane 1.52x0.8mm, normal (0.78,0.63,0), area 1.6mm2, adj f1,f2,f24,f46
  f50: plane 3.03x2.05mm, normal (-1,0,0), area 6.2mm2, adj f3,f4,f16,f53
  f51: plane 2.05x2.05mm, normal (0,-0.71,-0.71), area 0.7mm2, adj f6,f16,f52,f55
  f52: plane 2.04x0.26mm, normal (0,1,0), area 0.5mm2, adj f38,f51,f53,f55
  f53: plane 3.04x0.25mm, normal (0,1,0), area 0.8mm2, adj f50,f52,f54,f55
  f54: plane 3.51x0.25mm, normal (0,1,0), area 0.9mm2, adj f22,f44,f53,f55
  f55: plane 8.59x2.05mm, normal (1,0,0), area 13.4mm2, adj f16,f22,f51,f52,f53,f54
  f56: plane 7.55x0.76mm, normal (0,-1,0), area 5.7mm2, adj f2,f33,f40,f41,f42,f59
  f57: plane 0.77x0.7mm, normal (-1,0,0), area 0.4mm2, adj f0,f2,f17,f45,f59
  f58: plane 0.77x0.27mm, normal (-1,0,0), area 0mm2, adj f12,f19,f33,f43,f59
  f59: cylinder r=11.08mm len=11.08mm, axis (0,0,-1), area 117.2mm2, adj f2,f18,f33,f56,f57,f58
PLACE A rot(axis=(0,1,0),90deg) t=(18.34,52.04,21.16)mm
PLACE B rot(axis=(0,-1,0),90deg) t=(57.91,50.03,46.86)mm
PLACE C rot(axis=(0,1,0),90deg) t=(18.34,66.01,21.16)mm
PLACE D rot(axis=(0,-1,0),90deg) t=(57.97,64,47.07)mm
MATE fastened A.f57 <-> C.f44  axis (0,-1,0) through (25.19,14.59,2.99)mm
MATE fastened B.f12 <-> A.f21  axis (0,0,-1) through (50.76,54.82,0)mm
